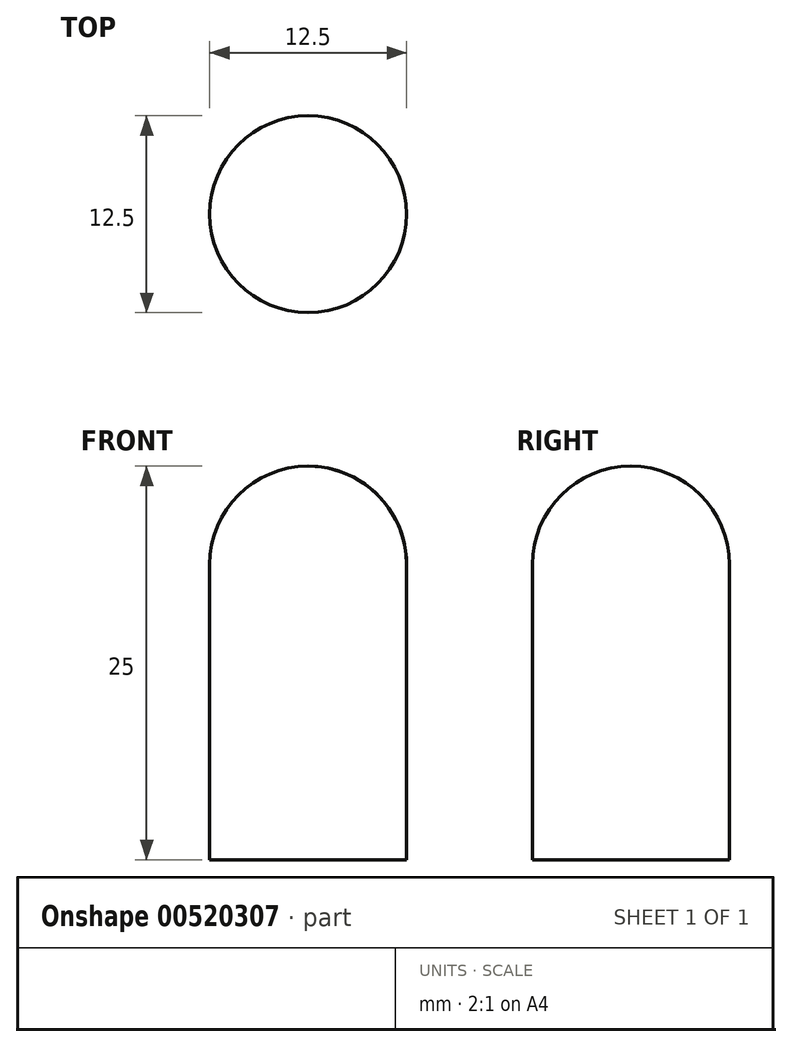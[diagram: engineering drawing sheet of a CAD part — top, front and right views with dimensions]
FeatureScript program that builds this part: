
annotation { "Feature Type Name" : "Feature", "Feature Type Description" : "" }
export const myFeature = defineFeature(function(context is Context, id is Id, definition is map)
    precondition{}
    {
        {
            var Q0;
            Q0=qCreatedBy(makeId("Top.planeOp"),FACE);
            var sketch = newSketch(context, id + "F0", { "sketchPlane" : qUnion([Q0])});
            skCircle(sketch, "E0", {"center": v(0, 0) * mm, "radius": 6.25 * mm});
            skSolve(sketch);
        }
        {
            var Q0;
            Q0 = qSketchRegion(id + "F0", true);
            extrude(context, id + "F1", {"entities" : qUnion([Q0]), "depth" : 25 * mm, "offsetDistance" : 25 * mm});
        }
        {
            var Q0;
            Q0=makeQuery(id+"F1.opExtrude","CAP_EDGE",EDGE,{"disambiguationData":[OSD([sQuery(id+"F0.wireOp",EDGE,"E0")])],"isStart":false});
            fillet(context, id + "F2", {"entities" : qUnion([Q0]), "radius" : 6.25 * mm, "tangentPropagation" : true, "allowEdgeOverflow" : false});
        }
    });
